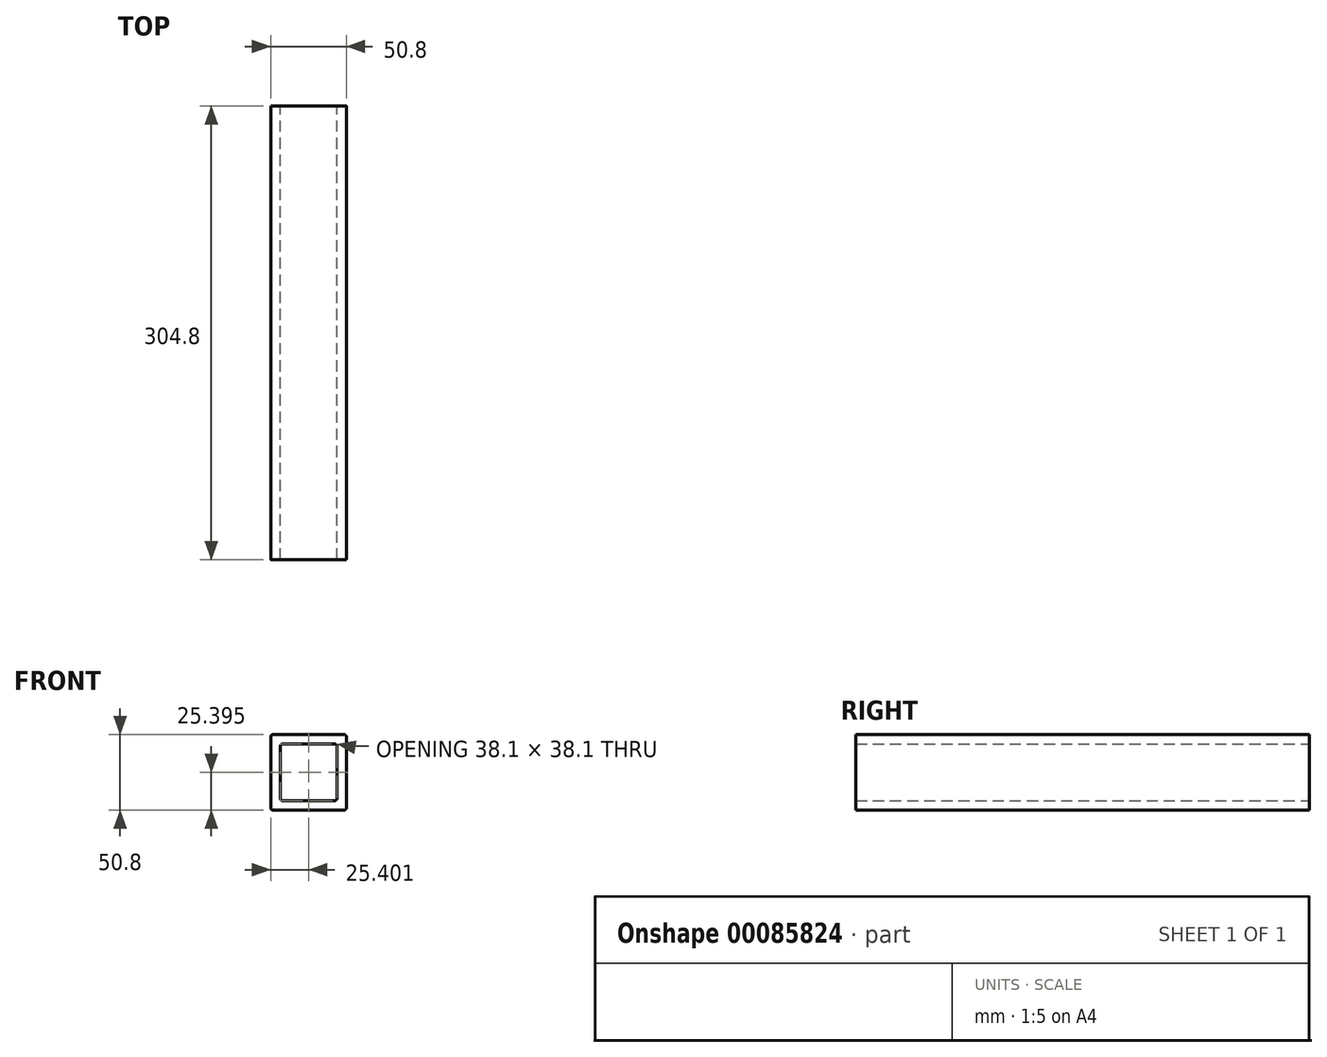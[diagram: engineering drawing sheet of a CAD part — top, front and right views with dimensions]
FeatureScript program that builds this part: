
annotation { "Feature Type Name" : "Feature", "Feature Type Description" : "" }
export const myFeature = defineFeature(function(context is Context, id is Id, definition is map)
    precondition{}
    {
        {
            var Q0;
            Q0=qCreatedBy(makeId("Front.planeOp"),FACE);
            var sketch = newSketch(context, id + "F0", { "sketchPlane" : qUnion([Q0])});
            skLineSegment(sketch, "E0.bottom", {"start": v(-33.24, 1.27) * mm, "end": v(-80.9, 1.27) * mm});
            skLineSegment(sketch, "E0.top", {"start": v(-33.24, 52.07) * mm, "end": v(-80.9, 52.07) * mm});
            skLineSegment(sketch, "E0.left", {"start": v(-31.67, 2.84) * mm, "end": v(-31.67, 50.5) * mm});
            skLineSegment(sketch, "E0.right", {"start": v(-82.47, 2.84) * mm, "end": v(-82.47, 50.5) * mm});
            skPoint(sketch, "E0.middle", {"position": v(-57.07, 26.67) * mm});
            skPoint(sketch, "E1.visualSharp", {"position": v(-82.47, 52.07) * mm});
            skArc(sketch, "E1.filletArc", {"start": v(-80.9, 52.07) * mm, "mid": v(-82, 51.6) * mm, "end": v(-82.47, 50.5) * mm});
            skPoint(sketch, "E2.visualSharp", {"position": v(-31.67, 52.07) * mm});
            skArc(sketch, "E2.filletArc", {"start": v(-31.67, 50.5) * mm, "mid": v(-32.13, 51.6) * mm, "end": v(-33.24, 52.07) * mm});
            skPoint(sketch, "E3.visualSharp", {"position": v(-31.67, 1.27) * mm});
            skArc(sketch, "E3.filletArc", {"start": v(-33.24, 1.27) * mm, "mid": v(-32.13, 1.73) * mm, "end": v(-31.67, 2.84) * mm});
            skPoint(sketch, "E4.visualSharp", {"position": v(-82.47, 1.27) * mm});
            skArc(sketch, "E4.filletArc", {"start": v(-82.47, 2.84) * mm, "mid": v(-82, 1.73) * mm, "end": v(-80.9, 1.27) * mm});
            skLineSegment(sketch, "E5.bottom", {"start": v(-74.54, 7.62) * mm, "end": v(-39.6, 7.62) * mm});
            skLineSegment(sketch, "E5.top", {"start": v(-74.54, 45.72) * mm, "end": v(-39.6, 45.72) * mm});
            skLineSegment(sketch, "E5.left", {"start": v(-76.12, 9.2) * mm, "end": v(-76.12, 44.14) * mm});
            skLineSegment(sketch, "E5.right", {"start": v(-38.02, 9.2) * mm, "end": v(-38.02, 44.14) * mm});
            skPoint(sketch, "E6.visualSharp", {"position": v(-76.12, 45.72) * mm});
            skArc(sketch, "E6.filletArc", {"start": v(-74.54, 45.72) * mm, "mid": v(-75.66, 45.25) * mm, "end": v(-76.12, 44.14) * mm});
            skPoint(sketch, "E7.visualSharp", {"position": v(-76.12, 7.62) * mm});
            skArc(sketch, "E7.filletArc", {"start": v(-76.12, 9.2) * mm, "mid": v(-75.66, 8.08) * mm, "end": v(-74.54, 7.62) * mm});
            skPoint(sketch, "E8.visualSharp", {"position": v(-38.02, 7.62) * mm});
            skArc(sketch, "E8.filletArc", {"start": v(-39.6, 7.62) * mm, "mid": v(-38.48, 8.08) * mm, "end": v(-38.02, 9.2) * mm});
            skPoint(sketch, "E9.visualSharp", {"position": v(-38.02, 45.72) * mm});
            skArc(sketch, "E9.filletArc", {"start": v(-38.02, 44.14) * mm, "mid": v(-38.48, 45.25) * mm, "end": v(-39.6, 45.72) * mm});
            skSolve(sketch);
        }
        {
            var Q0;
            Q0=makeQuery(id+"F0.imprint","IMPRINT",FACE,{"disambiguationData":[TD([[makeQuery(id+"F0.imprint","IMPRINT",EDGE,{"derivedFrom":sQuery(id+"F0.wireOp",EDGE,"E0.bottom")}),-1.0]])]});
            extrude(context, id + "F1", {"entities" : qUnion([Q0]), "depth" : 304.8 * mm, "offsetDistance" : 25.4 * mm});
        }
    });
